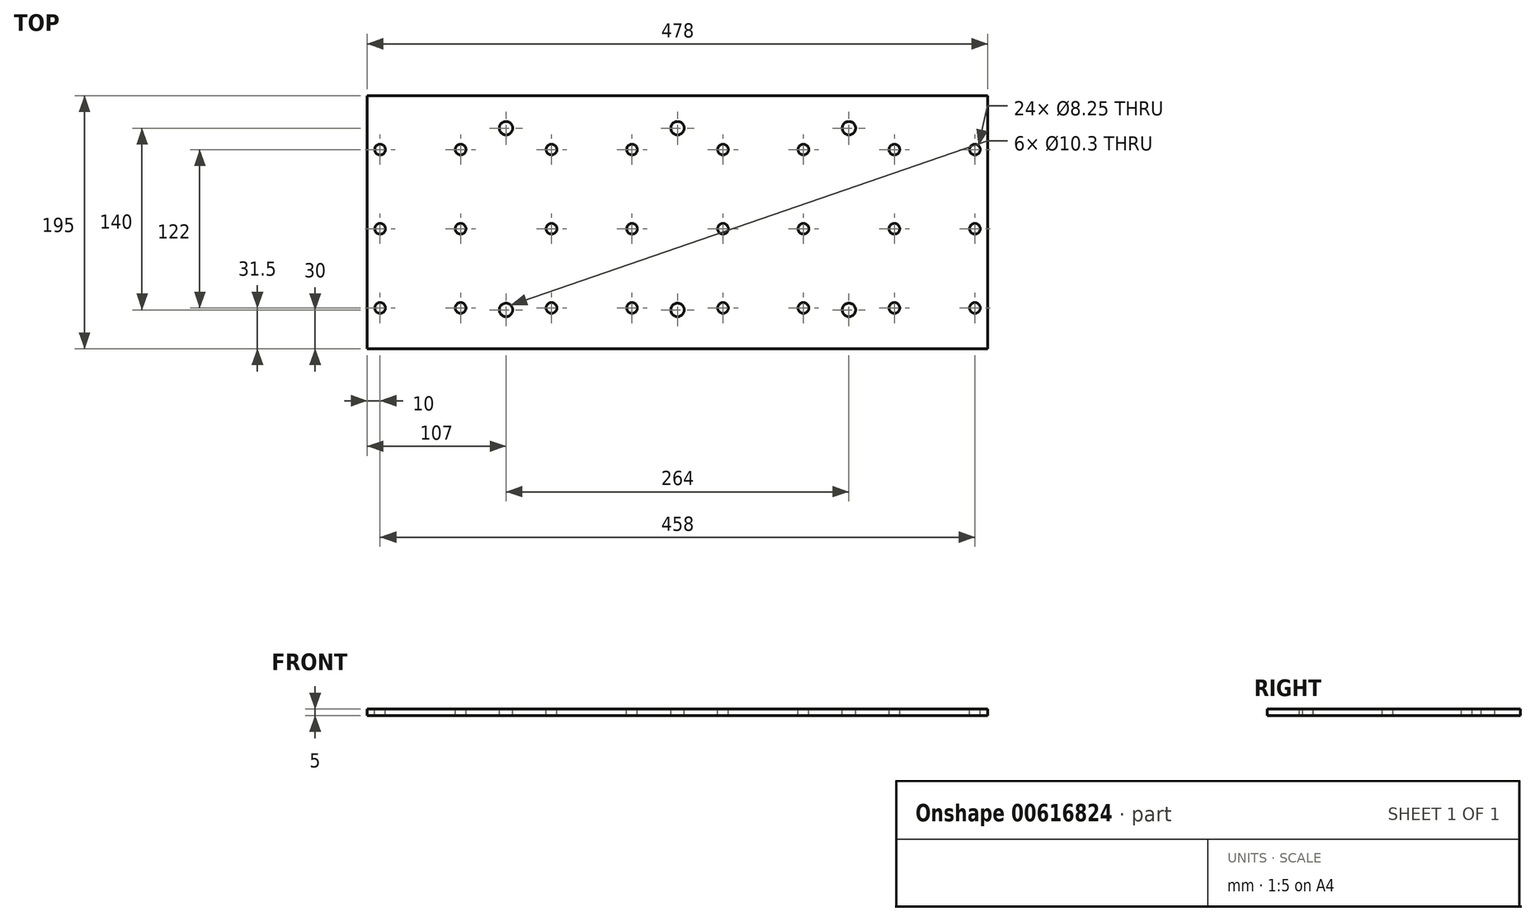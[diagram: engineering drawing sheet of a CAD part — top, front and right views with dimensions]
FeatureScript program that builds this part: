
annotation { "Feature Type Name" : "Feature", "Feature Type Description" : "" }
export const myFeature = defineFeature(function(context is Context, id is Id, definition is map)
    precondition{}
    {
        {
            var Q0;
            Q0=qCreatedBy(makeId("Top.planeOp"),FACE);
            var sketch = newSketch(context, id + "F0", { "sketchPlane" : qUnion([Q0])});
            skLineSegment(sketch, "E0.bottom", {"start": v(239, 97.5) * mm, "end": v(-239, 97.5) * mm});
            skLineSegment(sketch, "E0.top", {"start": v(239, -97.5) * mm, "end": v(-239, -97.5) * mm});
            skLineSegment(sketch, "E0.left", {"start": v(239, 97.5) * mm, "end": v(239, -97.5) * mm});
            skLineSegment(sketch, "E0.right", {"start": v(-239, 97.5) * mm, "end": v(-239, -97.5) * mm});
            skPoint(sketch, "E0.middle", {"position": v(0, 0) * mm});
            skPoint(sketch, "E1", {"position": v(-229, 56) * mm});
            skPoint(sketch, "E2", {"position": v(-229, -66) * mm});
            skPoint(sketch, "E3", {"position": v(-229, -5) * mm});
            skPoint(sketch, "E4.1.0.0", {"position": v(-167, 56) * mm});
            skPoint(sketch, "E4.1.0.1", {"position": v(-167, -5) * mm});
            skPoint(sketch, "E4.1.0.2", {"position": v(-167, -66) * mm});
            skLineSegment(sketch, "E4.direction1", {"start": v(-229, 56) * mm, "end": v(-167, 56) * mm, "construction": true});
            skPoint(sketch, "E5.1.0.0", {"position": v(-97, 56) * mm});
            skPoint(sketch, "E5.1.0.1", {"position": v(-97, -5) * mm});
            skPoint(sketch, "E5.1.0.2", {"position": v(-97, -66) * mm});
            skPoint(sketch, "E5.1.0.3", {"position": v(-35, -66) * mm});
            skPoint(sketch, "E5.1.0.4", {"position": v(-35, -5) * mm});
            skPoint(sketch, "E5.1.0.5", {"position": v(-35, 56) * mm});
            skPoint(sketch, "E5.2.0.0", {"position": v(35, 56) * mm});
            skPoint(sketch, "E5.2.0.1", {"position": v(35, -5) * mm});
            skPoint(sketch, "E5.2.0.2", {"position": v(35, -66) * mm});
            skPoint(sketch, "E5.2.0.3", {"position": v(97, -66) * mm});
            skPoint(sketch, "E5.2.0.4", {"position": v(97, -5) * mm});
            skPoint(sketch, "E5.2.0.5", {"position": v(97, 56) * mm});
            skPoint(sketch, "E5.3.0.0", {"position": v(167, 56) * mm});
            skPoint(sketch, "E5.3.0.1", {"position": v(167, -5) * mm});
            skPoint(sketch, "E5.3.0.2", {"position": v(167, -66) * mm});
            skPoint(sketch, "E5.3.0.3", {"position": v(229, -66) * mm});
            skPoint(sketch, "E5.3.0.4", {"position": v(229, -5) * mm});
            skPoint(sketch, "E5.3.0.5", {"position": v(229, 56) * mm});
            skLineSegment(sketch, "E5.direction1", {"start": v(-229, 56) * mm, "end": v(-97, 56) * mm, "construction": true});
            skPoint(sketch, "E6", {"position": v(-132, 72.5) * mm});
            skPoint(sketch, "E7", {"position": v(-132, -67.5) * mm});
            skPoint(sketch, "E8.1.0.0", {"position": v(0, 72.5) * mm});
            skPoint(sketch, "E8.1.0.1", {"position": v(0, -67.5) * mm});
            skPoint(sketch, "E8.2.0.0", {"position": v(132, 72.5) * mm});
            skPoint(sketch, "E8.2.0.1", {"position": v(132, -67.5) * mm});
            skLineSegment(sketch, "E8.direction1", {"start": v(-132, 72.5) * mm, "end": v(0, 72.5) * mm, "construction": true});
            skSolve(sketch);
        }
        {
            var Q0;
            Q0 = qSketchRegion(id + "F0", true);
            extrude(context, id + "F1", {"entities" : qUnion([Q0]), "depth" : 5 * mm, "offsetDistance" : 25 * mm});
        }
        {
            var Q0;
            Q0=sQuery(id+"F0.wireOp",VERTEX,"E1");
            var Q1;
            Q1=sQuery(id+"F0.wireOp",VERTEX,"E3");
            var Q2;
            Q2=sQuery(id+"F0.wireOp",VERTEX,"E2");
            var Q3;
            Q3=sQuery(id+"F0.wireOp",VERTEX,"E4.1.0.0");
            var Q4;
            Q4=sQuery(id+"F0.wireOp",VERTEX,"E4.1.0.1");
            var Q5;
            Q5=sQuery(id+"F0.wireOp",VERTEX,"E4.1.0.2");
            var Q6;
            Q6=sQuery(id+"F0.wireOp",VERTEX,"E5.1.0.2");
            var Q7;
            Q7=sQuery(id+"F0.wireOp",VERTEX,"E5.1.0.1");
            var Q8;
            Q8=sQuery(id+"F0.wireOp",VERTEX,"E5.1.0.0");
            var Q9;
            Q9=sQuery(id+"F0.wireOp",VERTEX,"E5.1.0.5");
            var Q10;
            Q10=sQuery(id+"F0.wireOp",VERTEX,"E5.1.0.4");
            var Q11;
            Q11=sQuery(id+"F0.wireOp",VERTEX,"E5.1.0.3");
            var Q12;
            Q12=sQuery(id+"F0.wireOp",VERTEX,"E5.2.0.2");
            var Q13;
            Q13=sQuery(id+"F0.wireOp",VERTEX,"E5.2.0.1");
            var Q14;
            Q14=sQuery(id+"F0.wireOp",VERTEX,"E5.2.0.0");
            var Q15;
            Q15=sQuery(id+"F0.wireOp",VERTEX,"E5.2.0.5");
            var Q16;
            Q16=sQuery(id+"F0.wireOp",VERTEX,"E5.2.0.4");
            var Q17;
            Q17=sQuery(id+"F0.wireOp",VERTEX,"E5.2.0.3");
            var Q18;
            Q18=sQuery(id+"F0.wireOp",VERTEX,"E5.3.0.2");
            var Q19;
            Q19=sQuery(id+"F0.wireOp",VERTEX,"E5.3.0.1");
            var Q20;
            Q20=sQuery(id+"F0.wireOp",VERTEX,"E5.3.0.0");
            var Q21;
            Q21=sQuery(id+"F0.wireOp",VERTEX,"E5.3.0.5");
            var Q22;
            Q22=sQuery(id+"F0.wireOp",VERTEX,"E5.3.0.4");
            var Q23;
            Q23=sQuery(id+"F0.wireOp",VERTEX,"E5.3.0.3");
            var Q24;
            Q24=makeQuery(id+"F1.opExtrude","SWEPT_BODY",BODY,{"disambiguationData":[OSD([sQuery(id+"F0.wireOp",EDGE,"E0.bottom"),sQuery(id+"F0.wireOp",EDGE,"E0.top"),sQuery(id+"F0.wireOp",EDGE,"E0.left"),sQuery(id+"F0.wireOp",EDGE,"E0.right")])]});
            hole(context, id + "F2", {"style" : HoleStyle.SIMPLE, "endStyle" : HoleEndStyle.THROUGH, "oppositeDirection" : true, "holeDiameter" : 8.25 * mm, "majorDiameter" : 10 * mm, "isTappedThrough" : true, "tappedDepth" : 12 * mm, "tapClearance" : 3, "locations" : qUnion([Q0, Q1, Q2, Q3, Q4, Q5, Q6, Q7, Q8, Q9, Q10, Q11, Q12, Q13, Q14, Q15, Q16, Q17, Q18, Q19, Q20, Q21, Q22, Q23]), "scope" : qUnion([Q24]), "startStyle" : HoleStartStyle.PART});
        }
        {
            var Q0;
            Q0=sQuery(id+"F0.wireOp",VERTEX,"E6");
            var Q1;
            Q1=sQuery(id+"F0.wireOp",VERTEX,"E7");
            var Q2;
            Q2=sQuery(id+"F0.wireOp",VERTEX,"E8.1.0.0");
            var Q3;
            Q3=sQuery(id+"F0.wireOp",VERTEX,"E8.1.0.1");
            var Q4;
            Q4=sQuery(id+"F0.wireOp",VERTEX,"E8.2.0.0");
            var Q5;
            Q5=sQuery(id+"F0.wireOp",VERTEX,"E8.2.0.1");
            var Q6;
            Q6=makeQuery(id+"F1.opExtrude","SWEPT_BODY",BODY,{"disambiguationData":[OSD([sQuery(id+"F0.wireOp",EDGE,"E0.bottom"),sQuery(id+"F0.wireOp",EDGE,"E0.top"),sQuery(id+"F0.wireOp",EDGE,"E0.left"),sQuery(id+"F0.wireOp",EDGE,"E0.right")])]});
            hole(context, id + "F3", {"style" : HoleStyle.SIMPLE, "endStyle" : HoleEndStyle.THROUGH, "oppositeDirection" : true, "standardTappedOrClearance" : lookupTablePath({ "standard" : "ISO", "engagement" : "75%", "pitch" : "1.75 mm", "size" : "M12", "type" : "Tapped" }), "standardBlindInLast" : lookupTablePath({ "standard" : "ISO", "engagement" : "75%", "pitch" : "1.75 mm", "size" : "M12", "type" : "Tapped" }), "holeDiameter" : 10.3 * mm, "majorDiameter" : 12 * mm, "showTappedDepth" : true, "isTappedThrough" : true, "tappedDepth" : 12 * mm, "tapClearance" : 3, "locations" : qUnion([Q0, Q1, Q2, Q3, Q4, Q5]), "scope" : qUnion([Q6]), "startStyle" : HoleStartStyle.PART});
        }
    });
